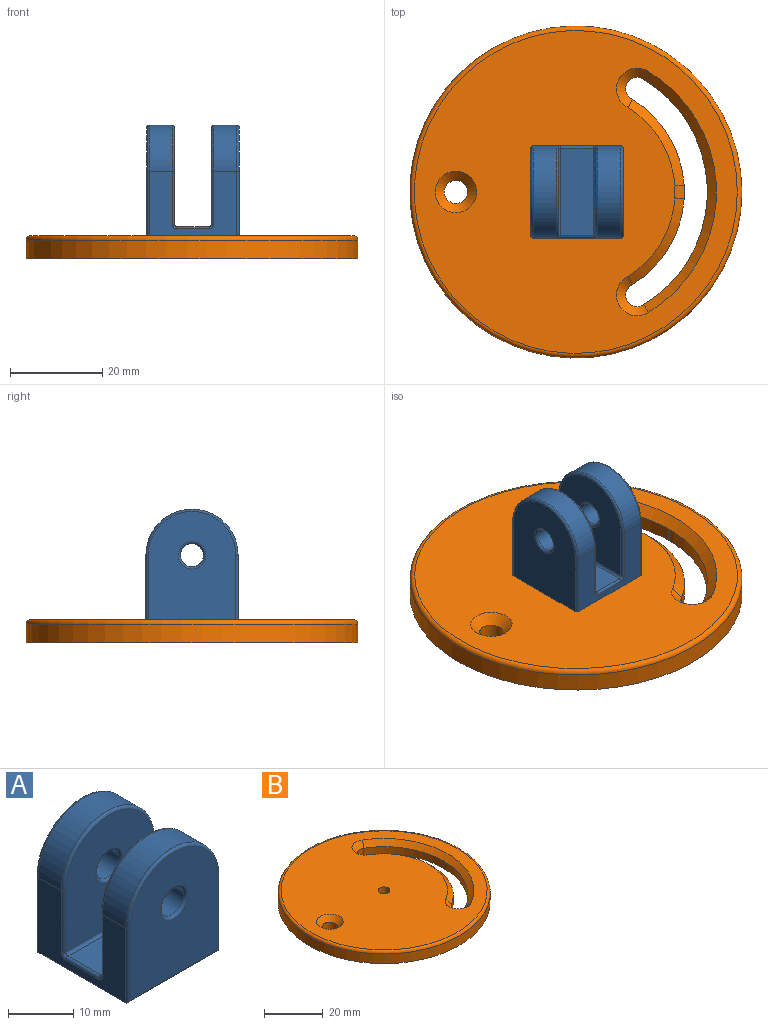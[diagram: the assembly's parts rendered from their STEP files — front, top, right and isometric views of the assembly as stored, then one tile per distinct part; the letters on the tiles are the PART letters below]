
ASSEMBLY  parts=2 mates=1
PART A: 37 faces, bbox 21.6x20x24.8 mm
  f0: plane 23x19mm, normal (0,-1,0), area 370mm2, adj f29,f32,f33,f34,f35
  f1: plane 21x19mm, normal (0,1,0), area 332mm2, adj f15,f19,f22,f23,f30
  f2: plane 21x19mm, normal (0,-1,0), area 332mm2, adj f16,f20,f24,f25,f31
  f3: plane 19x14mm, normal (1,0,0), area 153.9mm2, adj f6,f8,f9,f12,f15,f16,f17,f18
  f4: plane 23.5x19mm, normal (0,1,0), area 379.5mm2, adj f6,f12,f13,f14,f36
  f5: plane 19x14mm, normal (-1,0,0), area 153.9mm2, adj f6,f8,f9,f14,f23,f24,f26,f27
  f6: plane 20x19.5mm, normal (0,0,-1), area 389.9mm2, adj f3,f4,f5,f12,f14,f32
  f7: plane 19x7mm, normal (0,0,1), area 133mm2, adj f17,f22,f25,f28
  f8: cylinder r=10mm len=20mm, axis (0,1,0), area 157.1mm2, adj f3,f5,f13,f20
  f9: cylinder r=10mm len=20mm, axis (0,1,0), area 157.1mm2, adj f3,f5,f19,f35
  f10: cylinder r=2.5mm len=5mm, axis (0,1,0), area 78.5mm2, adj f31,f36
  f11: cylinder r=2.5mm len=5mm, axis (0,1,0), area 78.5mm2, adj f29,f30
  f12: cylinder r=0.5mm len=14mm, axis (0,0,1), area 11mm2, adj f3,f4,f6,f13
  f13: torus R=9.5mm, axis (0,-1,0), area 24.2mm2, adj f4,f8,f12,f14
  f14: cylinder r=0.5mm len=14mm, axis (0,0,-1), area 11mm2, adj f4,f5,f6,f13
  f15: cylinder r=0.5mm len=11.5mm, axis (0,0,1), area 9mm2, adj f1,f3,f18,f19
  f16: cylinder r=0.5mm len=11.5mm, axis (0,0,-1), area 9mm2, adj f2,f3,f20,f21
  f17: cylinder r=0.5mm len=7mm, axis (0,-1,0), area 5.5mm2, adj f3,f7,f18,f21
  f18: torus R=1mm, axis (1,0,0), area 0.8mm2, adj f3,f15,f17,f22
  f19: torus R=9.5mm, axis (0,-1,0), area 24.2mm2, adj f1,f9,f15,f23
  f20: torus R=9.5mm, axis (0,-1,0), area 24.2mm2, adj f2,f8,f16,f24
  f21: torus R=1mm, axis (1,0,0), area 0.8mm2, adj f3,f16,f17,f25
  f22: cylinder r=0.5mm len=19mm, axis (-1,0,0), area 14.9mm2, adj f1,f7,f18,f26
  f23: cylinder r=0.5mm len=11.5mm, axis (0,0,-1), area 9mm2, adj f1,f5,f19,f26
  f24: cylinder r=0.5mm len=11.5mm, axis (0,0,1), area 9mm2, adj f2,f5,f20,f27
  f25: cylinder r=0.5mm len=19mm, axis (1,0,0), area 14.9mm2, adj f2,f7,f21,f27
  f26: torus R=1mm, axis (1,0,0), area 0.8mm2, adj f5,f22,f23,f28
  f27: torus R=1mm, axis (1,0,0), area 0.8mm2, adj f5,f24,f25,f28
  f28: cylinder r=0.5mm len=7mm, axis (0,1,0), area 5.5mm2, adj f5,f7,f26,f27
  f29: torus R=3mm, axis (0,-1,0), area 13.2mm2, adj f0,f11
  f30: torus R=3mm, axis (0,-1,0), area 13.2mm2, adj f1,f11
  f31: torus R=3mm, axis (0,-1,0), area 13.2mm2, adj f2,f10
  f32: cylinder r=0.5mm len=20mm, axis (1,0,0), area 15.4mm2, adj f0,f6,f33,f34
  f33: cylinder r=0.5mm len=14mm, axis (0,0,-1), area 10.9mm2, adj f0,f3,f32,f35
  f34: cylinder r=0.5mm len=14mm, axis (0,0,1), area 10.9mm2, adj f0,f5,f32,f35
  f35: torus R=9.5mm, axis (0,-1,0), area 24.2mm2, adj f0,f9,f33,f34
  f36: torus R=3mm, axis (0,-1,0), area 13.2mm2, adj f4,f10
PART B: 19 faces, bbox 77.9x77.9x5 mm
  f0: cylinder r=28.5mm len=3mm, axis (0,0,-1), area 0.1mm2, adj f3,f7,f14
  f1: cylinder r=2.5mm len=3.02mm, axis (0,0,-1), area 0.3mm2, adj f4,f7,f15
  f2: cylinder r=2.5mm len=5mm, axis (0,0,-1), area 47.1mm2, adj f7,f17
  f3: cylinder r=2.5mm len=3mm, axis (0,0,-1), area 0.1mm2, adj f0,f7,f14
  f4: cylinder r=23.5mm len=3.02mm, axis (0,0,-1), area 0.3mm2, adj f1,f7,f15
  f5: cylinder r=36mm len=72mm, axis (0,0,-1), area 904.8mm2, adj f7,f8
  f6: plane 70x70mm, normal (0,0,1), area 3226mm2, adj f8,f13,f14,f15,f16,f17,f18
  f7: plane 72x72mm, normal (0,0,-1), area 3752.1mm2, adj f0,f1,f2,f3,f4,f5,f9,f10
  f8: torus R=35mm, axis (0,0,1), area 351.7mm2, adj f5,f6
  f9: cylinder r=28.5mm len=48.82mm, axis (0,0,1), area 175.9mm2, adj f7,f10,f12,f14
  f10: cylinder r=2.5mm len=4.78mm, axis (0,0,1), area 24.8mm2, adj f7,f9,f11,f13
  f11: cylinder r=23.52mm len=40.11mm, axis (0,0,1), area 144.1mm2, adj f7,f10,f12,f15
  f12: cylinder r=2.5mm len=4.78mm, axis (0,0,1), area 24.8mm2, adj f7,f9,f11,f16
  f13: cone r=2.5mm half-angle=45deg, axis (0,0,1), area 32.5mm2, adj f6,f10,f14,f15
  f14: cone r=30.5mm half-angle=45deg, axis (0,0,1), area 171.5mm2, adj f0,f3,f6,f9,f13,f16
  f15: cone r=23.52mm half-angle=45deg, axis (0,0,-1), area 129.8mm2, adj f1,f4,f6,f11,f13,f16
  f16: cone r=4.5mm half-angle=45deg, axis (0,0,1), area 32.5mm2, adj f6,f12,f14,f15
  f17: cone r=2.5mm half-angle=45deg, axis (0,0,1), area 62.2mm2, adj f2,f6
  f18: cylinder r=2mm len=5mm, axis (0,0,1), area 62.8mm2, adj f6,f7
PLACE A rot(axis=(0,0,1),90deg) t=(-1.83,-1.45,2.12)mm
PLACE B t=(-2.08,-1.45,-2.88)mm
MATE fastened A.f6 <-> B.f5  axis (0,0,-1) through (-2.08,-1.45,2.12)mm
